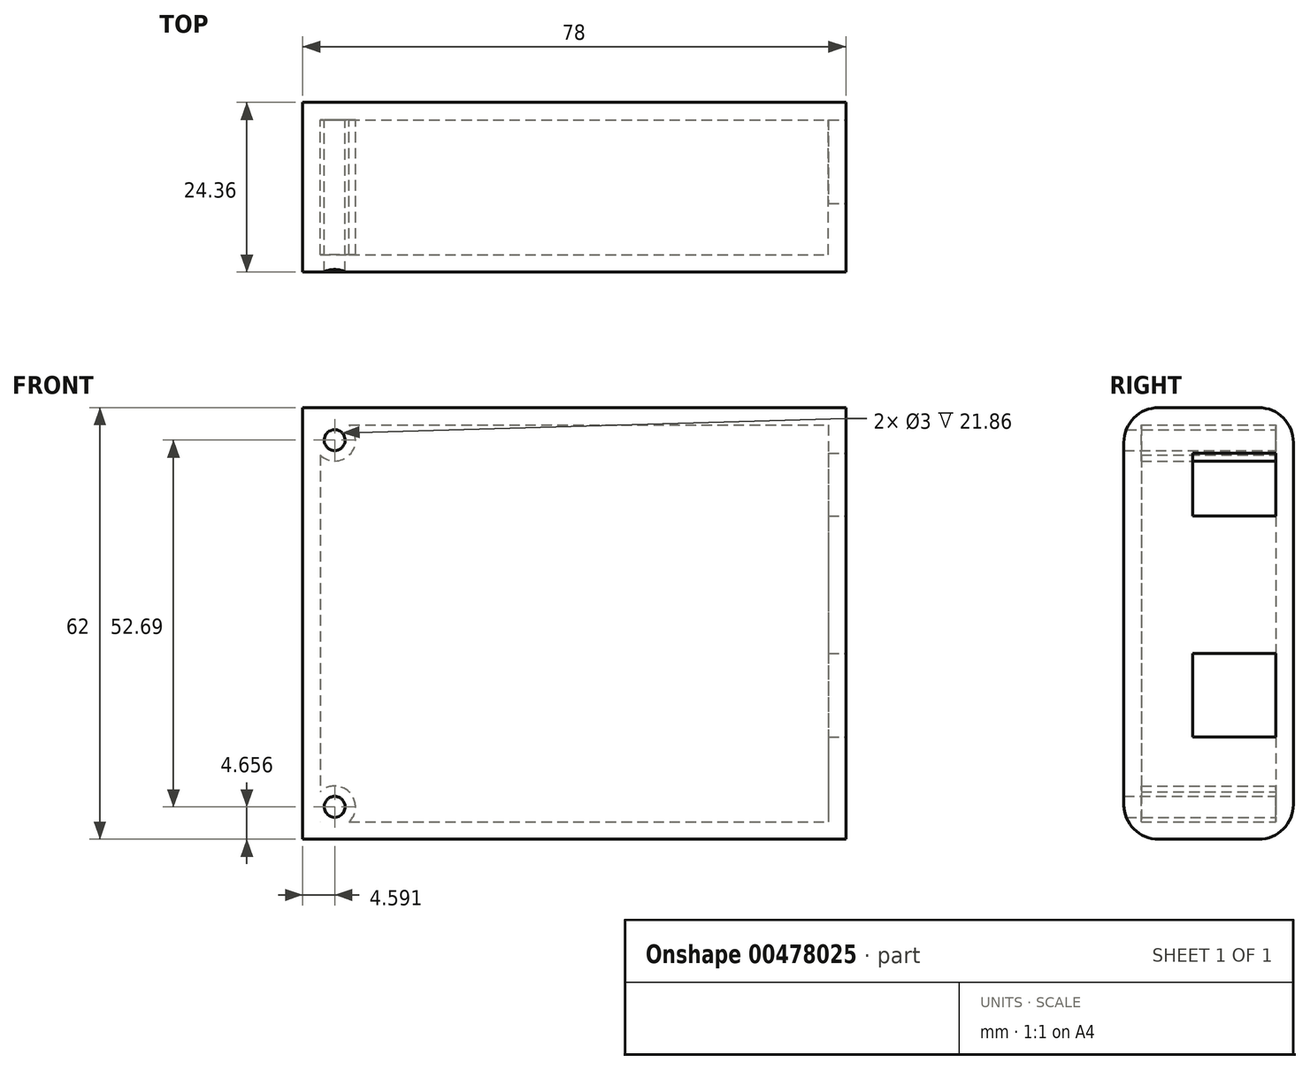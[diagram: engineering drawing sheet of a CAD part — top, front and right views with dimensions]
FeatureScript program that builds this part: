
annotation { "Feature Type Name" : "Feature", "Feature Type Description" : "" }
export const myFeature = defineFeature(function(context is Context, id is Id, definition is map)
    precondition{}
    {
        {
            var Q0;
            Q0=qCreatedBy(makeId("Front.planeOp"),FACE);
            var sketch = newSketch(context, id + "F0", { "sketchPlane" : qUnion([Q0])});
            skLineSegment(sketch, "E0.bottom", {"start": v(-35.67, 36.7) * mm, "end": v(37.33, 36.7) * mm});
            skLineSegment(sketch, "E0.top", {"start": v(-35.67, -20.3) * mm, "end": v(37.33, -20.3) * mm});
            skLineSegment(sketch, "E0.left", {"start": v(-35.67, 36.7) * mm, "end": v(-35.67, -20.3) * mm});
            skLineSegment(sketch, "E0.right", {"start": v(37.33, 36.7) * mm, "end": v(37.33, -20.3) * mm});
            skSolve(sketch);
        }
        {
            var Q0;
            Q0=makeQuery(id+"F0.imprint","IMPRINT",FACE,{"disambiguationData":[TD([[makeQuery(id+"F0.imprint","IMPRINT",EDGE,{"derivedFrom":sQuery(id+"F0.wireOp",EDGE,"E0.bottom")}),-1.0]])]});
            extrude(context, id + "F1", {"entities" : qUnion([Q0]), "depth" : 9.68 * mm});
        }
        {
            var Q0;
            Q0=makeQuery(id+"F1.opExtrude","CAP_FACE",FACE,{"disambiguationData":[OSD([sQuery(id+"F0.wireOp",EDGE,"E0.bottom"),sQuery(id+"F0.wireOp",EDGE,"E0.top"),sQuery(id+"F0.wireOp",EDGE,"E0.left"),sQuery(id+"F0.wireOp",EDGE,"E0.right")])],"isStart":false});
            shell(context, id + "F2", {"entities" : qUnion([Q0]), "thickness" : 2.5 * mm, "oppositeDirection" : true});
        }
        {
            var Q0;
            Q0=makeQuery(id+"F1.opExtrude","CAP_EDGE",EDGE,{"disambiguationData":[OSD([sQuery(id+"F0.wireOp",EDGE,"E0.top")])],"isStart":true});
            fillet(context, id + "F3", {"entities" : qUnion([Q0]), "radius" : 5 * mm, "tangentPropagation" : true, "allowEdgeOverflow" : false});
        }
        {
            var Q0;
            Q0=makeQuery(id+"F1.opExtrude","CAP_EDGE",EDGE,{"disambiguationData":[OSD([sQuery(id+"F0.wireOp",EDGE,"E0.bottom")])],"isStart":true});
            fillet(context, id + "F4", {"entities" : qUnion([Q0]), "radius" : 5 * mm, "tangentPropagation" : true, "allowEdgeOverflow" : false});
        }
        {
            var Q0;
            Q0=makeQuery(id+"F2.opShell","OFFSET_FACE",FACE,{"disambiguationData":[OSD([sQuery(id+"F0.wireOp",EDGE,"E0.bottom"),sQuery(id+"F0.wireOp",EDGE,"E0.top"),sQuery(id+"F0.wireOp",EDGE,"E0.left"),sQuery(id+"F0.wireOp",EDGE,"E0.right")])]});
            var sketch = newSketch(context, id + "F5", { "sketchPlane" : qUnion([Q0])});
            skLineSegment(sketch, "E1.bottom", {"start": v(29.6, 32.67) * mm, "end": v(43.74, 32.67) * mm});
            skLineSegment(sketch, "E1.top", {"start": v(29.6, 23.62) * mm, "end": v(43.74, 23.62) * mm});
            skLineSegment(sketch, "E1.left", {"start": v(29.6, 32.67) * mm, "end": v(29.6, 23.62) * mm});
            skLineSegment(sketch, "E1.right", {"start": v(43.74, 32.67) * mm, "end": v(43.74, 23.62) * mm});
            skSolve(sketch);
        }
        {
            var Q0;
            Q0=makeQuery(id+"F17.boolean.opBoolean","MERGE",FACE,{"derivedFrom":[makeQuery(id+"F15.boolean.opBoolean","MERGE",FACE,{"derivedFrom":[makeQuery(id+"F2.opShell","OFFSET_FACE",FACE,{"disambiguationData":[OSD([sQuery(id+"F0.wireOp",EDGE,"E0.bottom"),sQuery(id+"F0.wireOp",EDGE,"E0.top"),sQuery(id+"F0.wireOp",EDGE,"E0.left"),sQuery(id+"F0.wireOp",EDGE,"E0.right")])]}),makeQuery(id+"F15.opExtrude","CAP_FACE",FACE,{"disambiguationData":[OSD([sQuery(id+"F5.wireOp",EDGE,"E1.bottom"),sQuery(id+"F5.wireOp",EDGE,"E1.top"),sQuery(id+"F5.wireOp",EDGE,"E1.left"),sQuery(id+"F5.wireOp",EDGE,"E1.right")])],"isStart":true})]}),makeQuery(id+"F17.opExtrude","CAP_FACE",FACE,{"disambiguationData":[OSD([sQuery(id+"F16.wireOp",EDGE,"E6.bottom"),sQuery(id+"F16.wireOp",EDGE,"E6.top"),sQuery(id+"F16.wireOp",EDGE,"E6.left"),sQuery(id+"F16.wireOp",EDGE,"E6.right")])],"isStart":true})]});
            var sketch = newSketch(context, id + "F6", { "sketchPlane" : qUnion([Q0])});
            skCircle(sketch, "E2", {"center": v(-33.58, 34.55) * mm, "radius": 3 * mm});
            skSolve(sketch);
        }
        {
            var Q0;
            Q0 = qSketchRegion(id + "F6", true);
            extrude(context, id + "F7", {"entities" : qUnion([Q0]), "operationType" : NewBodyOperationType.ADD, "depth" : 9.68 * mm});
        }
        {
            var Q0;
            Q0=makeQuery(id+"F17.boolean.opBoolean","MERGE",FACE,{"derivedFrom":[makeQuery(id+"F15.boolean.opBoolean","MERGE",FACE,{"derivedFrom":[makeQuery(id+"F2.opShell","OFFSET_FACE",FACE,{"disambiguationData":[OSD([sQuery(id+"F0.wireOp",EDGE,"E0.bottom"),sQuery(id+"F0.wireOp",EDGE,"E0.top"),sQuery(id+"F0.wireOp",EDGE,"E0.left"),sQuery(id+"F0.wireOp",EDGE,"E0.right")])]}),makeQuery(id+"F15.opExtrude","CAP_FACE",FACE,{"disambiguationData":[OSD([sQuery(id+"F5.wireOp",EDGE,"E1.bottom"),sQuery(id+"F5.wireOp",EDGE,"E1.top"),sQuery(id+"F5.wireOp",EDGE,"E1.left"),sQuery(id+"F5.wireOp",EDGE,"E1.right")])],"isStart":true})]}),makeQuery(id+"F17.opExtrude","CAP_FACE",FACE,{"disambiguationData":[OSD([sQuery(id+"F16.wireOp",EDGE,"E6.bottom"),sQuery(id+"F16.wireOp",EDGE,"E6.top"),sQuery(id+"F16.wireOp",EDGE,"E6.left"),sQuery(id+"F16.wireOp",EDGE,"E6.right")])],"isStart":true})]});
            var sketch = newSketch(context, id + "F8", { "sketchPlane" : qUnion([Q0])});
            skCircle(sketch, "E3", {"center": v(-33.58, 34.55) * mm, "radius": 1.5 * mm});
            skSolve(sketch);
        }
        {
            var Q0;
            Q0=makeQuery(id+"F17.boolean.opBoolean","MERGE",FACE,{"derivedFrom":[makeQuery(id+"F15.boolean.opBoolean","MERGE",FACE,{"derivedFrom":[makeQuery(id+"F2.opShell","OFFSET_FACE",FACE,{"disambiguationData":[OSD([sQuery(id+"F0.wireOp",EDGE,"E0.bottom"),sQuery(id+"F0.wireOp",EDGE,"E0.top"),sQuery(id+"F0.wireOp",EDGE,"E0.left"),sQuery(id+"F0.wireOp",EDGE,"E0.right")])]}),makeQuery(id+"F15.opExtrude","CAP_FACE",FACE,{"disambiguationData":[OSD([sQuery(id+"F5.wireOp",EDGE,"E1.bottom"),sQuery(id+"F5.wireOp",EDGE,"E1.top"),sQuery(id+"F5.wireOp",EDGE,"E1.left"),sQuery(id+"F5.wireOp",EDGE,"E1.right")])],"isStart":true})]}),makeQuery(id+"F17.opExtrude","CAP_FACE",FACE,{"disambiguationData":[OSD([sQuery(id+"F16.wireOp",EDGE,"E6.bottom"),sQuery(id+"F16.wireOp",EDGE,"E6.top"),sQuery(id+"F16.wireOp",EDGE,"E6.left"),sQuery(id+"F16.wireOp",EDGE,"E6.right")])],"isStart":true})]});
            var sketch = newSketch(context, id + "F9", { "sketchPlane" : qUnion([Q0])});
            skCircle(sketch, "E4", {"center": v(-33.58, -18.14) * mm, "radius": 3 * mm});
            skSolve(sketch);
        }
        {
            var Q0;
            Q0 = qSketchRegion(id + "F9", true);
            var Q1;
            {var subQ0=sQuery(id+"F0.wireOp",EDGE,"E0.left");var subQ1=sQuery(id+"F0.wireOp",EDGE,"E0.bottom");var subQ2=sQuery(id+"F0.wireOp",EDGE,"E0.top");var subQ3=sQuery(id+"F0.wireOp",EDGE,"E0.right");Q1=makeQuery(id+"F7.boolean.opBoolean","MERGE",FACE,{"derivedFrom":[makeQuery(id+"F17.boolean.opBoolean","SPLIT",FACE,{"disambiguationData":[TD([makeQuery(id+"F1.opExtrude","SWEPT_FACE",FACE,{"disambiguationData":[OSD([subQ1])]})])],"derivedFrom":makeQuery(id+"F1.opExtrude","CAP_FACE",FACE,{"disambiguationData":[OSD([subQ1,subQ2,subQ0,subQ3])],"isStart":false})}),makeQuery(id+"F7.opExtrude","CAP_FACE",FACE,{"disambiguationData":[OSD([sQuery(id+"F6.wireOp",EDGE,"E2")])],"isStart":false})]});}
            extrude(context, id + "F10", {"entities" : qUnion([Q0]), "operationType" : NewBodyOperationType.ADD, "endBound" : BoundingType.UP_TO_SURFACE, "endBoundEntityFace" : qUnion([Q1]), "depth" : 9.8 * mm});
        }
        {
            var Q0;
            Q0=makeQuery(id+"F1.opExtrude","SWEPT_BODY",BODY,{"disambiguationData":[OSD([sQuery(id+"F0.wireOp",EDGE,"E0.bottom"),sQuery(id+"F0.wireOp",EDGE,"E0.top"),sQuery(id+"F0.wireOp",EDGE,"E0.left"),sQuery(id+"F0.wireOp",EDGE,"E0.right")])]});
            var Q1;
            {var subQ0=sQuery(id+"F0.wireOp",EDGE,"E0.left");var subQ1=sQuery(id+"F0.wireOp",EDGE,"E0.bottom");var subQ2=sQuery(id+"F0.wireOp",EDGE,"E0.top");var subQ3=sQuery(id+"F0.wireOp",EDGE,"E0.right");Q1=makeQuery(id+"F10.boolean.opBoolean","MERGE",FACE,{"derivedFrom":[makeQuery(id+"F7.boolean.opBoolean","MERGE",FACE,{"derivedFrom":[makeQuery(id+"F17.boolean.opBoolean","SPLIT",FACE,{"disambiguationData":[TD([makeQuery(id+"F1.opExtrude","SWEPT_FACE",FACE,{"disambiguationData":[OSD([subQ1])]})])],"derivedFrom":makeQuery(id+"F1.opExtrude","CAP_FACE",FACE,{"disambiguationData":[OSD([subQ1,subQ2,subQ0,subQ3])],"isStart":false})}),makeQuery(id+"F7.opExtrude","CAP_FACE",FACE,{"disambiguationData":[OSD([sQuery(id+"F6.wireOp",EDGE,"E2")])],"isStart":false})]}),makeQuery(id+"F10.opExtrude","CAP_FACE",FACE,{"disambiguationData":[OSD([sQuery(id+"F9.wireOp",EDGE,"E4")])],"isStart":false})]});}
            mirror(context, id + "F11", {"entities" : qUnion([Q0]), "mirrorPlane" : qUnion([Q1])});
        }
        {
            var Q0;
            Q0 = qSketchRegion(id + "F8", true);
            extrude(context, id + "F12", {"entities" : qUnion([Q0]), "operationType" : NewBodyOperationType.ADD, "depth" : 13.3 * mm});
        }
        {
            var Q0;
            {var subQ2=sQuery(id+"F5.wireOp",EDGE,"E1.left");Q0=makeQuery(id+"F5.imprint","IMPRINT",FACE,{"disambiguationData":[TD([[makeQuery(id+"F5.imprint","IMPRINT",EDGE,{"derivedFrom":subQ2}),-1.0]])]});}
            var sketch = newSketch(context, id + "F13", { "sketchPlane" : qUnion([Q0])});
            skCircle(sketch, "E5", {"center": v(-33.58, -18.14) * mm, "radius": 1.5 * mm});
            skSolve(sketch);
        }
        {
            var Q0;
            Q0 = qSketchRegion(id + "F13", true);
            var Q1;
            {var subQ0=sQuery(id+"F0.wireOp",EDGE,"E0.left");var subQ1=sQuery(id+"F0.wireOp",EDGE,"E0.bottom");var subQ2=sQuery(id+"F0.wireOp",EDGE,"E0.top");var subQ3=sQuery(id+"F0.wireOp",EDGE,"E0.right");Q1=makeQuery(id+"F7.boolean.opBoolean","MERGE",FACE,{"derivedFrom":[makeQuery(id+"F17.boolean.opBoolean","SPLIT",FACE,{"disambiguationData":[TD([makeQuery(id+"F1.opExtrude","SWEPT_FACE",FACE,{"disambiguationData":[OSD([subQ1])]})])],"derivedFrom":makeQuery(id+"F1.opExtrude","CAP_FACE",FACE,{"disambiguationData":[OSD([subQ1,subQ2,subQ0,subQ3])],"isStart":false})}),makeQuery(id+"F7.opExtrude","CAP_FACE",FACE,{"disambiguationData":[OSD([sQuery(id+"F6.wireOp",EDGE,"E2")])],"isStart":false})]});}
            extrude(context, id + "F14", {"entities" : qUnion([Q0]), "operationType" : NewBodyOperationType.ADD, "endBoundEntityFace" : qUnion([Q1]), "depth" : 13 * mm});
        }
        {
            var Q0;
            Q0 = qSketchRegion(id + "F5", true);
            extrude(context, id + "F15", {"entities" : qUnion([Q0]), "operationType" : NewBodyOperationType.REMOVE, "depth" : 12 * mm});
        }
        {
            var Q0;
            Q0=makeQuery(id+"F15.boolean.opBoolean","MERGE",FACE,{"derivedFrom":[makeQuery(id+"F2.opShell","OFFSET_FACE",FACE,{"disambiguationData":[OSD([sQuery(id+"F0.wireOp",EDGE,"E0.bottom"),sQuery(id+"F0.wireOp",EDGE,"E0.top"),sQuery(id+"F0.wireOp",EDGE,"E0.left"),sQuery(id+"F0.wireOp",EDGE,"E0.right")])]}),makeQuery(id+"F15.opExtrude","CAP_FACE",FACE,{"disambiguationData":[OSD([sQuery(id+"F5.wireOp",EDGE,"E1.bottom"),sQuery(id+"F5.wireOp",EDGE,"E1.top"),sQuery(id+"F5.wireOp",EDGE,"E1.left"),sQuery(id+"F5.wireOp",EDGE,"E1.right")])],"isStart":true})]});
            var sketch = newSketch(context, id + "F16", { "sketchPlane" : qUnion([Q0])});
            skLineSegment(sketch, "E6.bottom", {"start": v(33.53, 3.92) * mm, "end": v(44.58, 3.92) * mm});
            skLineSegment(sketch, "E6.top", {"start": v(33.53, -8.13) * mm, "end": v(44.58, -8.13) * mm});
            skLineSegment(sketch, "E6.left", {"start": v(33.53, 3.92) * mm, "end": v(33.53, -8.13) * mm});
            skLineSegment(sketch, "E6.right", {"start": v(44.58, 3.92) * mm, "end": v(44.58, -8.13) * mm});
            skSolve(sketch);
        }
        {
            var Q0;
            Q0 = qSketchRegion(id + "F16", true);
            extrude(context, id + "F17", {"entities" : qUnion([Q0]), "operationType" : NewBodyOperationType.REMOVE, "depth" : 12 * mm});
        }
        {
            var Q0;
            Q0 = qSketchRegion(id + "F8", true);
            extrude(context, id + "F18", {"entities" : qUnion([Q0]), "operationType" : NewBodyOperationType.REMOVE, "depth" : 25 * mm});
        }
        {
            var Q0;
            Q0 = qSketchRegion(id + "F13", true);
            extrude(context, id + "F19", {"entities" : qUnion([Q0]), "operationType" : NewBodyOperationType.REMOVE, "depth" : 25 * mm});
        }
    });
